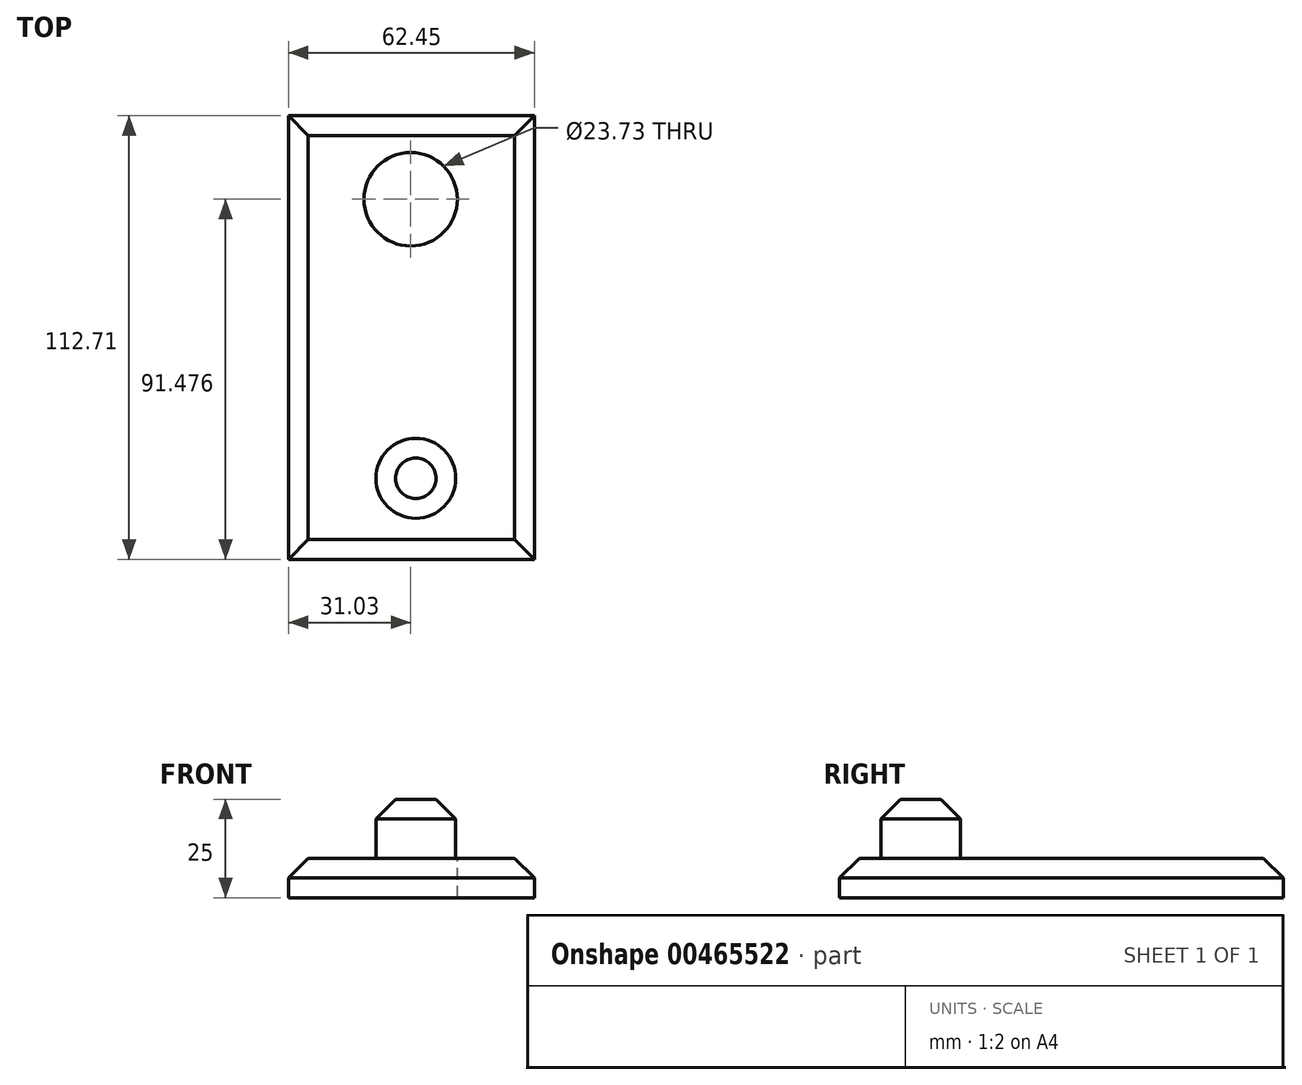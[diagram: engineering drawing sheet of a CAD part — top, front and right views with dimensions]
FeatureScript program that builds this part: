
annotation { "Feature Type Name" : "Feature", "Feature Type Description" : "" }
export const myFeature = defineFeature(function(context is Context, id is Id, definition is map)
    precondition{}
    {
        {
            var Q0;
            Q0=qCreatedBy(makeId("Top.planeOp"),FACE);
            var sketch = newSketch(context, id + "F0", { "sketchPlane" : qUnion([Q0])});
            skLineSegment(sketch, "E0.bottom", {"start": v(0, -62.45) * mm, "end": v(62.45, -62.45) * mm});
            skLineSegment(sketch, "E0.top", {"start": v(0, 50.26) * mm, "end": v(62.45, 50.26) * mm});
            skLineSegment(sketch, "E0.left", {"start": v(0, -62.45) * mm, "end": v(0, 50.26) * mm});
            skLineSegment(sketch, "E0.right", {"start": v(62.45, -62.45) * mm, "end": v(62.45, 50.26) * mm});
            skSolve(sketch);
        }
        {
            var Q0;
            Q0 = qSketchRegion(id + "F0", true);
            extrude(context, id + "F1", {"entities" : qUnion([Q0]), "depth" : 10 * mm});
        }
        {
            var Q0;
            Q0=makeQuery(id+"F1.opExtrude","CAP_FACE",FACE,{"disambiguationData":[OSD([sQuery(id+"F0.wireOp",EDGE,"E0.bottom"),sQuery(id+"F0.wireOp",EDGE,"E0.top"),sQuery(id+"F0.wireOp",EDGE,"E0.left"),sQuery(id+"F0.wireOp",EDGE,"E0.right")])],"isStart":false});
            var sketch = newSketch(context, id + "F2", { "sketchPlane" : qUnion([Q0])});
            skSolve(sketch);
        }
        {
            var Q0;
            Q0=makeQuery(id+"F2.imprint","IMPRINT",FACE,{"disambiguationData":[TD([[makeQuery(id+"F2.imprint","IMPRINT",EDGE,{"derivedFrom":makeQuery(id+"F1.opExtrude","CAP_EDGE",EDGE,{"disambiguationData":[OSD([sQuery(id+"F0.wireOp",EDGE,"E0.bottom")])],"isStart":false})}),1.0]])]});
            var sketch = newSketch(context, id + "F3", { "sketchPlane" : qUnion([Q0])});
            skCircle(sketch, "E1", {"center": v(31.03, 29.03) * mm, "radius": 11.86 * mm});
            skSolve(sketch);
        }
        {
            var Q0;
            Q0 = qSketchRegion(id + "F3", true);
            extrude(context, id + "F4", {"entities" : qUnion([Q0]), "operationType" : NewBodyOperationType.REMOVE, "oppositeDirection" : true, "depth" : 25 * mm});
        }
        {
            var Q0;
            Q0=makeQuery(id+"F2.imprint","IMPRINT",FACE,{"disambiguationData":[TD([[makeQuery(id+"F2.imprint","IMPRINT",EDGE,{"derivedFrom":makeQuery(id+"F1.opExtrude","CAP_EDGE",EDGE,{"disambiguationData":[OSD([sQuery(id+"F0.wireOp",EDGE,"E0.bottom")])],"isStart":false})}),1.0]])]});
            var sketch = newSketch(context, id + "F5", { "sketchPlane" : qUnion([Q0])});
            skSolve(sketch);
        }
        {
            var Q0;
            Q0=qCreatedBy(makeId("Top.planeOp"),FACE);
            var sketch = newSketch(context, id + "F6", { "sketchPlane" : qUnion([Q0])});
            skCircle(sketch, "E2", {"center": v(32.35, -41.87) * mm, "radius": 10.14 * mm});
            skSolve(sketch);
        }
        {
            var Q0;
            Q0=makeQuery(id+"F6.imprint","IMPRINT",FACE,{"disambiguationData":[TD([[makeQuery(id+"F6.imprint","IMPRINT",EDGE,{"derivedFrom":sQuery(id+"F6.wireOp",EDGE,"E2")}),1.0]])]});
            extrude(context, id + "F7", {"entities" : qUnion([Q0]), "operationType" : NewBodyOperationType.ADD, "depth" : 25 * mm});
        }
        {
            var Q0;
            Q0=makeQuery(id+"F5.imprint","IMPRINT",FACE,{"disambiguationData":[TD([[makeQuery(id+"F5.imprint","IMPRINT",EDGE,{"derivedFrom":makeQuery(id+"F2.imprint","IMPRINT",EDGE,{"derivedFrom":makeQuery(id+"F1.opExtrude","CAP_EDGE",EDGE,{"disambiguationData":[OSD([sQuery(id+"F0.wireOp",EDGE,"E0.bottom")])],"isStart":false})})}),1.0]])]});
            var sketch = newSketch(context, id + "F8", { "sketchPlane" : qUnion([Q0])});
            skSolve(sketch);
        }
        {
            var Q0;
            Q0=makeQuery(id+"F1.opExtrude","CAP_EDGE",EDGE,{"disambiguationData":[OSD([sQuery(id+"F0.wireOp",EDGE,"E0.top")])],"isStart":false});
            chamfer(context, id + "F9", {"entities" : qUnion([Q0]), "width" : 5 * mm, "tangentPropagation" : true});
        }
        {
            var Q0;
            Q0=makeQuery(id+"F1.opExtrude","CAP_EDGE",EDGE,{"disambiguationData":[OSD([sQuery(id+"F0.wireOp",EDGE,"E0.right")])],"isStart":false});
            var Q1;
            Q1=makeQuery(id+"F1.opExtrude","CAP_EDGE",EDGE,{"disambiguationData":[OSD([sQuery(id+"F0.wireOp",EDGE,"E0.left")])],"isStart":false});
            var Q2;
            Q2=makeQuery(id+"F1.opExtrude","CAP_EDGE",EDGE,{"disambiguationData":[OSD([sQuery(id+"F0.wireOp",EDGE,"E0.bottom")])],"isStart":false});
            var Q3;
            Q3=makeQuery(id+"F7.opExtrude","CAP_EDGE",EDGE,{"disambiguationData":[OSD([sQuery(id+"F6.wireOp",EDGE,"E2")])],"isStart":false});
            var Q4;
            Q4=makeQuery(id+"F4.boolean.opBoolean","COPY",EDGE,{"derivedFrom":makeQuery(id+"F4.opExtrude","CAP_EDGE",EDGE,{"disambiguationData":[OSD([sQuery(id+"F3.wireOp",EDGE,"E1")])],"isStart":true})});
            chamfer(context, id + "F10", {"entities" : qUnion([Q0, Q1, Q2, Q3, Q4]), "width" : 5 * mm, "tangentPropagation" : true});
        }
    });
